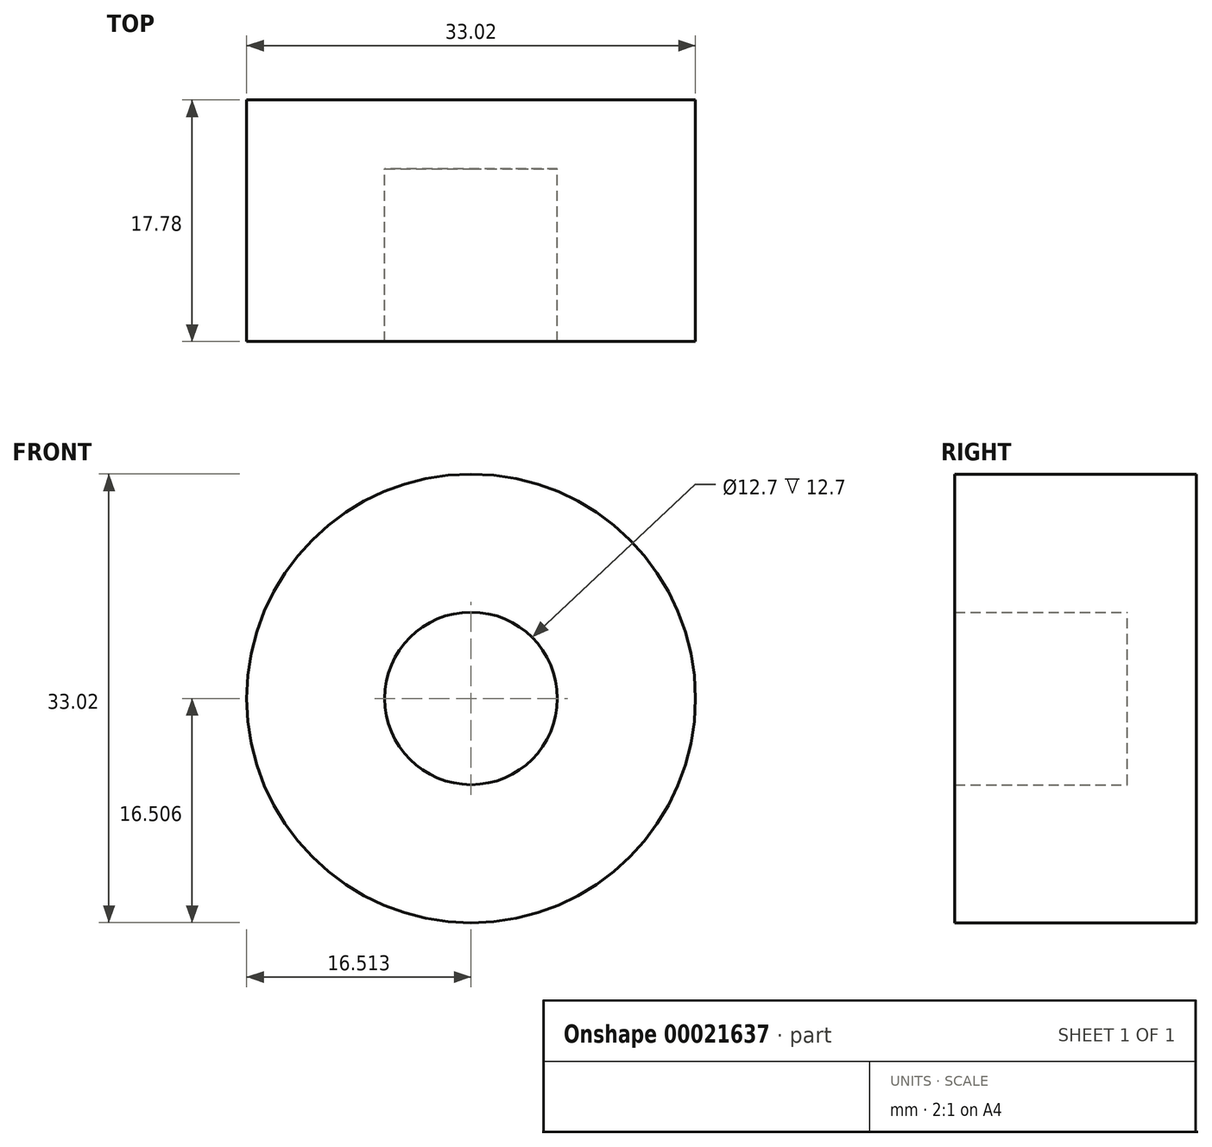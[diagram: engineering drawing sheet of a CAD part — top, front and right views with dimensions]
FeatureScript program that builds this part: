
annotation { "Feature Type Name" : "Feature", "Feature Type Description" : "" }
export const myFeature = defineFeature(function(context is Context, id is Id, definition is map)
    precondition{}
    {
        {
            var Q0;
            Q0=qCreatedBy(makeId("Front.planeOp"),FACE);
            var sketch = newSketch(context, id + "F0", { "sketchPlane" : qUnion([Q0])});
            skCircle(sketch, "E0", {"center": v(-41.94, 25.84) * mm, "radius": 6.35 * mm});
            skCircle(sketch, "E1", {"center": v(-41.94, 25.84) * mm, "radius": 16.51 * mm});
            skSolve(sketch);
        }
        {
            var Q0;
            Q0=makeQuery(id+"F0.imprint","IMPRINT",FACE,{"disambiguationData":[TD([[makeQuery(id+"F0.imprint","IMPRINT",EDGE,{"derivedFrom":sQuery(id+"F0.wireOp",EDGE,"E0")}),-1.0]])]});
            extrude(context, id + "F1", {"entities" : qUnion([Q0]), "depth" : 12.7 * mm});
        }
        {
            var Q0;
            Q0=makeQuery(id+"F0.imprint","IMPRINT",FACE,{"disambiguationData":[TD([[makeQuery(id+"F0.imprint","IMPRINT",EDGE,{"derivedFrom":sQuery(id+"F0.wireOp",EDGE,"E0")}),1.0]])]});
            var Q1;
            Q1=makeQuery(id+"F0.imprint","IMPRINT",FACE,{"disambiguationData":[TD([[makeQuery(id+"F0.imprint","IMPRINT",EDGE,{"derivedFrom":sQuery(id+"F0.wireOp",EDGE,"E0")}),-1.0]])]});
            extrude(context, id + "F2", {"entities" : qUnion([Q0, Q1]), "operationType" : NewBodyOperationType.ADD, "oppositeDirection" : true, "depth" : 5.08 * mm});
        }
    });
